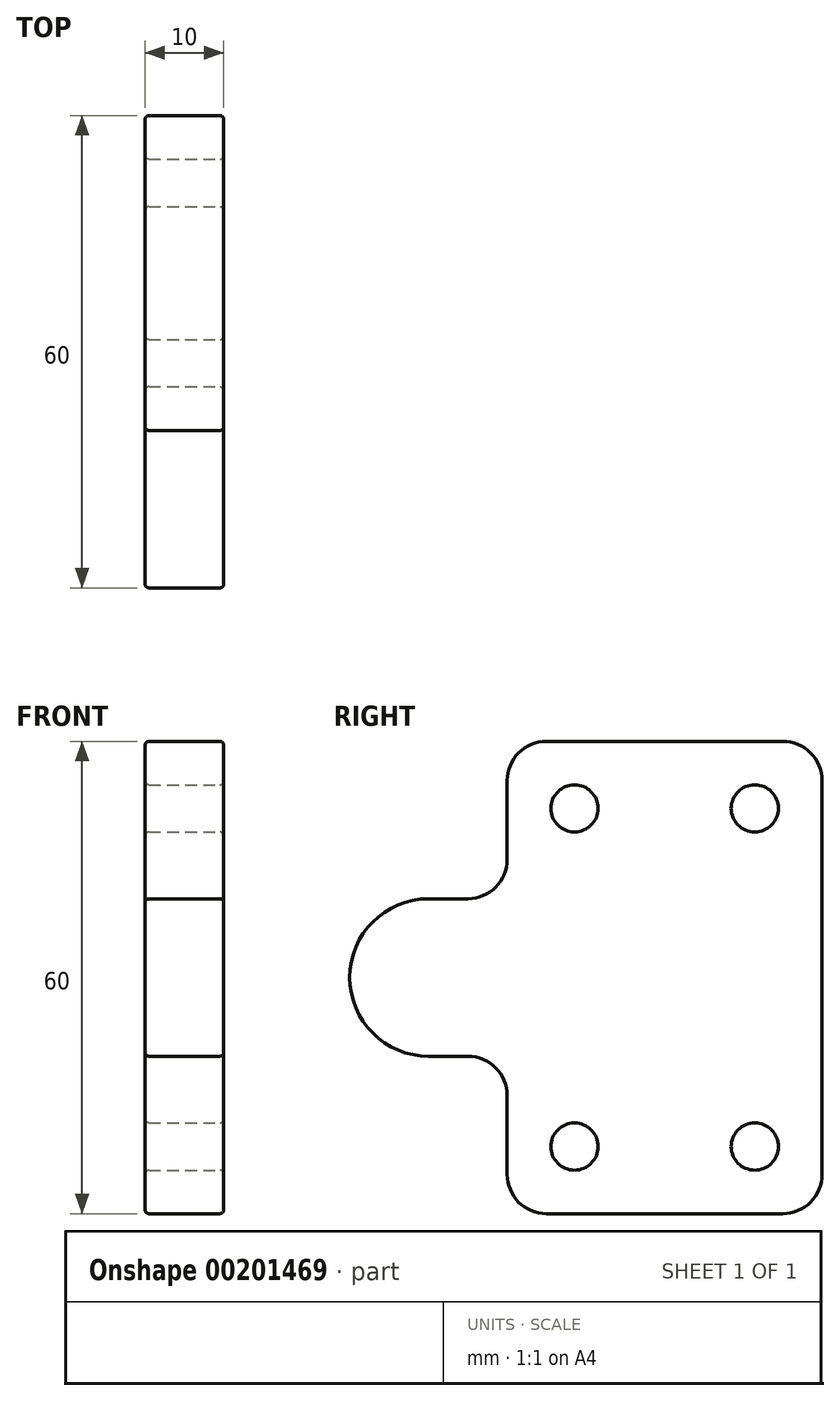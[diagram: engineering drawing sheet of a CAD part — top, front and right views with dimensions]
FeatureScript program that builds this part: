
annotation { "Feature Type Name" : "Feature", "Feature Type Description" : "" }
export const myFeature = defineFeature(function(context is Context, id is Id, definition is map)
    precondition{}
    {
        {
            var Q0;
            Q0=qCreatedBy(makeId("Right.planeOp"),FACE);
            var sketch = newSketch(context, id + "F0", { "sketchPlane" : qUnion([Q0])});
            skLineSegment(sketch, "E0.bottom", {"start": v(-20, -30) * mm, "end": v(20, -30) * mm});
            skLineSegment(sketch, "E0.top", {"start": v(-20, 30) * mm, "end": v(20, 30) * mm});
            skLineSegment(sketch, "E0.left", {"start": v(-20, -30) * mm, "end": v(-20, -15) * mm});
            skLineSegment(sketch, "E0.right", {"start": v(20, -30) * mm, "end": v(20, 30) * mm});
            skPoint(sketch, "E0.middle", {"position": v(0, 0) * mm});
            skArc(sketch, "E1", {"start": v(-30, 10) * mm, "mid": v(-40, 0) * mm, "end": v(-30, -10) * mm});
            skLineSegment(sketch, "E2", {"start": v(-30, 10) * mm, "end": v(-25, 10) * mm});
            skLineSegment(sketch, "E3", {"start": v(-30, -10) * mm, "end": v(-25, -10) * mm});
            skLineSegment(sketch, "E4.trimOffspring", {"start": v(-20, 15) * mm, "end": v(-20, 30) * mm});
            skPoint(sketch, "E5.visualSharp", {"position": v(-20, -10) * mm});
            skArc(sketch, "E5.filletArc", {"start": v(-20, -15) * mm, "mid": v(-21.46, -11.46) * mm, "end": v(-25, -10) * mm});
            skPoint(sketch, "E6.visualSharp", {"position": v(-20, 10) * mm});
            skArc(sketch, "E6.filletArc", {"start": v(-25, 10) * mm, "mid": v(-21.46, 11.46) * mm, "end": v(-20, 15) * mm});
            skSolve(sketch);
        }
        {
            var Q0;
            Q0=makeQuery(id+"F0.imprint","IMPRINT",FACE,{"disambiguationData":[TD([[makeQuery(id+"F0.imprint","IMPRINT",EDGE,{"derivedFrom":sQuery(id+"F0.wireOp",EDGE,"E0.bottom")}),1.0]])]});
            extrude(context, id + "F1", {"entities" : qUnion([Q0]), "depth" : 10 * mm});
        }
        {
            var Q0;
            Q0=makeQuery(id+"F1.opExtrude","SWEPT_EDGE",EDGE,{"disambiguationData":[OSD([sQuery(id+"F0.wireOp",EDGE,"E0.top"),sQuery(id+"F0.wireOp",EDGE,"E4.trimOffspring")])]});
            var Q1;
            Q1=makeQuery(id+"F1.opExtrude","SWEPT_EDGE",EDGE,{"disambiguationData":[OSD([sQuery(id+"F0.wireOp",EDGE,"E0.top"),sQuery(id+"F0.wireOp",EDGE,"E0.right")])]});
            var Q2;
            Q2=makeQuery(id+"F1.opExtrude","SWEPT_EDGE",EDGE,{"disambiguationData":[OSD([sQuery(id+"F0.wireOp",EDGE,"E0.bottom"),sQuery(id+"F0.wireOp",EDGE,"E0.right")])]});
            var Q3;
            Q3=makeQuery(id+"F1.opExtrude","SWEPT_EDGE",EDGE,{"disambiguationData":[OSD([sQuery(id+"F0.wireOp",EDGE,"E0.bottom"),sQuery(id+"F0.wireOp",EDGE,"E0.left")])]});
            fillet(context, id + "F2", {"entities" : qUnion([Q0, Q1, Q2, Q3]), "radius" : 5 * mm, "tangentPropagation" : true, "allowEdgeOverflow" : false});
        }
        {
            var Q0;
            Q0=makeQuery(id+"F1.opExtrude","CAP_FACE",FACE,{"disambiguationData":[OSD([sQuery(id+"F0.wireOp",EDGE,"E0.bottom"),sQuery(id+"F0.wireOp",EDGE,"E0.top"),sQuery(id+"F0.wireOp",EDGE,"E0.left"),sQuery(id+"F0.wireOp",EDGE,"E0.right"),sQuery(id+"F0.wireOp",EDGE,"E1"),sQuery(id+"F0.wireOp",EDGE,"E2"),sQuery(id+"F0.wireOp",EDGE,"E3"),sQuery(id+"F0.wireOp",EDGE,"E4.trimOffspring"),sQuery(id+"F0.wireOp",EDGE,"E5.filletArc"),sQuery(id+"F0.wireOp",EDGE,"E6.filletArc")])],"isStart":false});
            var sketch = newSketch(context, id + "F3", { "sketchPlane" : qUnion([Q0])});
            skPoint(sketch, "E7", {"position": v(7.84, 8.3) * mm});
            skSolve(sketch);
        }
        {
            var Q0;
            {var subQ6=sQuery(id+"F0.wireOp",EDGE,"E1");Q0=makeQuery(id+"F3.imprint","IMPRINT",FACE,{"disambiguationData":[TD([[makeQuery(id+"F3.imprint","IMPRINT",EDGE,{"derivedFrom":makeQuery(id+"F1.opExtrude","CAP_EDGE",EDGE,{"disambiguationData":[OSD([subQ6])],"isStart":false})}),1.0]])]});}
            var sketch = newSketch(context, id + "F4", { "sketchPlane" : qUnion([Q0])});
            skPoint(sketch, "E8", {"position": v(-11.45, 21.48) * mm});
            skLineSegment(sketch, "E9", {"start": v(-43.3, 0) * mm, "end": v(25.62, 0) * mm, "construction": true});
            skLineSegment(sketch, "E10", {"start": v(0, 34.37) * mm, "end": v(0, -34.73) * mm, "construction": true});
            skPoint(sketch, "E11.MirrorP", {"position": v(-11.45, -21.48) * mm});
            skPoint(sketch, "E12.MirrorP", {"position": v(11.45, -21.48) * mm});
            skPoint(sketch, "E13.MirrorP", {"position": v(11.45, 21.48) * mm});
            skSolve(sketch);
        }
        {
            var Q0;
            Q0=sQuery(id+"F4.wireOp",VERTEX,"E8");
            var Q1;
            Q1=sQuery(id+"F4.wireOp",VERTEX,"E13.MirrorP");
            var Q2;
            Q2=sQuery(id+"F4.wireOp",VERTEX,"E12.MirrorP");
            var Q3;
            Q3=sQuery(id+"F4.wireOp",VERTEX,"E11.MirrorP");
            var Q4;
            Q4=makeQuery(id+"F1.opExtrude","SWEPT_BODY",BODY,{"disambiguationData":[OSD([sQuery(id+"F0.wireOp",EDGE,"E0.bottom"),sQuery(id+"F0.wireOp",EDGE,"E0.top"),sQuery(id+"F0.wireOp",EDGE,"E0.left"),sQuery(id+"F0.wireOp",EDGE,"E0.right"),sQuery(id+"F0.wireOp",EDGE,"E1"),sQuery(id+"F0.wireOp",EDGE,"E2"),sQuery(id+"F0.wireOp",EDGE,"E3"),sQuery(id+"F0.wireOp",EDGE,"E4.trimOffspring"),sQuery(id+"F0.wireOp",EDGE,"E5.filletArc"),sQuery(id+"F0.wireOp",EDGE,"E6.filletArc")])]});
            hole(context, id + "F5", {"style" : HoleStyle.SIMPLE, "endStyle" : HoleEndStyle.THROUGH, "holeDiameter" : 6 * mm, "locations" : qUnion([Q0, Q1, Q2, Q3]), "scope" : qUnion([Q4]), "isTappedThrough" : true});
        }
        {
            var Q0;
            Q0=makeQuery(id+"F2.opFillet","BLEND_FACE",FACE,{"disambiguationData":[OSD([sQuery(id+"F0.wireOp",EDGE,"E0.bottom"),sQuery(id+"F0.wireOp",EDGE,"E0.left")])]});
            var Q1;
            {var subQ0=sQuery(id+"F0.wireOp",EDGE,"E0.left");var subQ1=sQuery(id+"F0.wireOp",EDGE,"E0.bottom");Q1=makeQuery(id+"F2.opFillet","BLEND_EDGE",EDGE,{"blendedFrom":[makeQuery(id+"F1.opExtrude","SWEPT_EDGE",EDGE,{"disambiguationData":[OSD([subQ1,subQ0])]}),makeQuery(id+"F1.opExtrude","CAP_FACE",FACE,{"disambiguationData":[OSD([subQ1,sQuery(id+"F0.wireOp",EDGE,"E0.top"),subQ0,sQuery(id+"F0.wireOp",EDGE,"E0.right"),sQuery(id+"F0.wireOp",EDGE,"E1"),sQuery(id+"F0.wireOp",EDGE,"E2"),sQuery(id+"F0.wireOp",EDGE,"E3"),sQuery(id+"F0.wireOp",EDGE,"E4.trimOffspring"),sQuery(id+"F0.wireOp",EDGE,"E5.filletArc"),sQuery(id+"F0.wireOp",EDGE,"E6.filletArc")])],"isStart":false})],"blendedInto":[makeQuery(id+"F1.opExtrude","CAP_FACE",FACE,{"disambiguationData":[OSD([subQ1,sQuery(id+"F0.wireOp",EDGE,"E0.top"),subQ0,sQuery(id+"F0.wireOp",EDGE,"E0.right"),sQuery(id+"F0.wireOp",EDGE,"E1"),sQuery(id+"F0.wireOp",EDGE,"E2"),sQuery(id+"F0.wireOp",EDGE,"E3"),sQuery(id+"F0.wireOp",EDGE,"E4.trimOffspring"),sQuery(id+"F0.wireOp",EDGE,"E5.filletArc"),sQuery(id+"F0.wireOp",EDGE,"E6.filletArc")])],"isStart":false})]});}
            var Q2;
            Q2=makeQuery(id+"F2.opFillet","BLEND_FACE",FACE,{"disambiguationData":[OSD([sQuery(id+"F0.wireOp",EDGE,"E0.top"),sQuery(id+"F0.wireOp",EDGE,"E4.trimOffspring")])]});
            var Q3;
            {var subQ0=sQuery(id+"F0.wireOp",EDGE,"E0.right");var subQ1=sQuery(id+"F0.wireOp",EDGE,"E0.bottom");Q3=makeQuery(id+"F2.opFillet","BLEND_EDGE",EDGE,{"blendedFrom":[makeQuery(id+"F1.opExtrude","SWEPT_EDGE",EDGE,{"disambiguationData":[OSD([subQ1,subQ0])]}),makeQuery(id+"F1.opExtrude","CAP_FACE",FACE,{"disambiguationData":[OSD([subQ1,sQuery(id+"F0.wireOp",EDGE,"E0.top"),sQuery(id+"F0.wireOp",EDGE,"E0.left"),subQ0,sQuery(id+"F0.wireOp",EDGE,"E1"),sQuery(id+"F0.wireOp",EDGE,"E2"),sQuery(id+"F0.wireOp",EDGE,"E3"),sQuery(id+"F0.wireOp",EDGE,"E4.trimOffspring"),sQuery(id+"F0.wireOp",EDGE,"E5.filletArc"),sQuery(id+"F0.wireOp",EDGE,"E6.filletArc")])],"isStart":false})],"blendedInto":[makeQuery(id+"F1.opExtrude","CAP_FACE",FACE,{"disambiguationData":[OSD([subQ1,sQuery(id+"F0.wireOp",EDGE,"E0.top"),sQuery(id+"F0.wireOp",EDGE,"E0.left"),subQ0,sQuery(id+"F0.wireOp",EDGE,"E1"),sQuery(id+"F0.wireOp",EDGE,"E2"),sQuery(id+"F0.wireOp",EDGE,"E3"),sQuery(id+"F0.wireOp",EDGE,"E4.trimOffspring"),sQuery(id+"F0.wireOp",EDGE,"E5.filletArc"),sQuery(id+"F0.wireOp",EDGE,"E6.filletArc")])],"isStart":false})]});}
            var Q4;
            Q4=makeQuery(id+"F2.opFillet","BLEND_FACE",FACE,{"disambiguationData":[OSD([sQuery(id+"F0.wireOp",EDGE,"E0.top"),sQuery(id+"F0.wireOp",EDGE,"E0.right")])]});
            var Q5;
            Q5=makeQuery(id+"F1.opExtrude","SWEPT_FACE",FACE,{"disambiguationData":[OSD([sQuery(id+"F0.wireOp",EDGE,"E1")])]});
            var Q6;
            Q6=makeQuery(id+"F1.opExtrude","SWEPT_FACE",FACE,{"disambiguationData":[OSD([sQuery(id+"F0.wireOp",EDGE,"E2")])]});
            var Q7;
            Q7=makeQuery(id+"F1.opExtrude","SWEPT_FACE",FACE,{"disambiguationData":[OSD([sQuery(id+"F0.wireOp",EDGE,"E0.bottom")])]});
            var Q8;
            Q8=makeQuery(id+"F1.opExtrude","SWEPT_FACE",FACE,{"disambiguationData":[OSD([sQuery(id+"F0.wireOp",EDGE,"E0.top")])]});
            var Q9;
            Q9=makeQuery(id+"F1.opExtrude","SWEPT_FACE",FACE,{"disambiguationData":[OSD([sQuery(id+"F0.wireOp",EDGE,"E3")])]});
            var Q10;
            Q10=makeQuery(id+"F1.opExtrude","SWEPT_FACE",FACE,{"disambiguationData":[OSD([sQuery(id+"F0.wireOp",EDGE,"E5.filletArc")])]});
            var Q11;
            {var subQ0=sQuery(id+"F0.wireOp",EDGE,"E0.right");var subQ1=sQuery(id+"F0.wireOp",EDGE,"E0.top");Q11=makeQuery(id+"F2.opFillet","BLEND_EDGE",EDGE,{"blendedFrom":[makeQuery(id+"F1.opExtrude","SWEPT_EDGE",EDGE,{"disambiguationData":[OSD([subQ1,subQ0])]}),makeQuery(id+"F1.opExtrude","CAP_FACE",FACE,{"disambiguationData":[OSD([sQuery(id+"F0.wireOp",EDGE,"E0.bottom"),subQ1,sQuery(id+"F0.wireOp",EDGE,"E0.left"),subQ0,sQuery(id+"F0.wireOp",EDGE,"E1"),sQuery(id+"F0.wireOp",EDGE,"E2"),sQuery(id+"F0.wireOp",EDGE,"E3"),sQuery(id+"F0.wireOp",EDGE,"E4.trimOffspring"),sQuery(id+"F0.wireOp",EDGE,"E5.filletArc"),sQuery(id+"F0.wireOp",EDGE,"E6.filletArc")])],"isStart":false})],"blendedInto":[makeQuery(id+"F1.opExtrude","CAP_FACE",FACE,{"disambiguationData":[OSD([sQuery(id+"F0.wireOp",EDGE,"E0.bottom"),subQ1,sQuery(id+"F0.wireOp",EDGE,"E0.left"),subQ0,sQuery(id+"F0.wireOp",EDGE,"E1"),sQuery(id+"F0.wireOp",EDGE,"E2"),sQuery(id+"F0.wireOp",EDGE,"E3"),sQuery(id+"F0.wireOp",EDGE,"E4.trimOffspring"),sQuery(id+"F0.wireOp",EDGE,"E5.filletArc"),sQuery(id+"F0.wireOp",EDGE,"E6.filletArc")])],"isStart":false})]});}
            var Q12;
            Q12=makeQuery(id+"F1.opExtrude","CAP_EDGE",EDGE,{"disambiguationData":[OSD([sQuery(id+"F0.wireOp",EDGE,"E1")])],"isStart":false});
            var Q13;
            Q13=makeQuery(id+"F2.opFillet","BLEND_FACE",FACE,{"disambiguationData":[OSD([sQuery(id+"F0.wireOp",EDGE,"E0.bottom"),sQuery(id+"F0.wireOp",EDGE,"E0.right")])]});
            var Q14;
            Q14=makeQuery(id+"F1.opExtrude","CAP_EDGE",EDGE,{"disambiguationData":[OSD([sQuery(id+"F0.wireOp",EDGE,"E5.filletArc")])],"isStart":false});
            var Q15;
            Q15=makeQuery(id+"F1.opExtrude","SWEPT_FACE",FACE,{"disambiguationData":[OSD([sQuery(id+"F0.wireOp",EDGE,"E0.left")])]});
            var Q16;
            {var subQ0=sQuery(id+"F0.wireOp",EDGE,"E4.trimOffspring");var subQ1=sQuery(id+"F0.wireOp",EDGE,"E0.top");Q16=makeQuery(id+"F2.opFillet","BLEND_EDGE",EDGE,{"blendedFrom":[makeQuery(id+"F1.opExtrude","SWEPT_EDGE",EDGE,{"disambiguationData":[OSD([subQ1,subQ0])]}),makeQuery(id+"F1.opExtrude","CAP_FACE",FACE,{"disambiguationData":[OSD([sQuery(id+"F0.wireOp",EDGE,"E0.bottom"),subQ1,sQuery(id+"F0.wireOp",EDGE,"E0.left"),sQuery(id+"F0.wireOp",EDGE,"E0.right"),sQuery(id+"F0.wireOp",EDGE,"E1"),sQuery(id+"F0.wireOp",EDGE,"E2"),sQuery(id+"F0.wireOp",EDGE,"E3"),subQ0,sQuery(id+"F0.wireOp",EDGE,"E5.filletArc"),sQuery(id+"F0.wireOp",EDGE,"E6.filletArc")])],"isStart":false})],"blendedInto":[makeQuery(id+"F1.opExtrude","CAP_FACE",FACE,{"disambiguationData":[OSD([sQuery(id+"F0.wireOp",EDGE,"E0.bottom"),subQ1,sQuery(id+"F0.wireOp",EDGE,"E0.left"),sQuery(id+"F0.wireOp",EDGE,"E0.right"),sQuery(id+"F0.wireOp",EDGE,"E1"),sQuery(id+"F0.wireOp",EDGE,"E2"),sQuery(id+"F0.wireOp",EDGE,"E3"),subQ0,sQuery(id+"F0.wireOp",EDGE,"E5.filletArc"),sQuery(id+"F0.wireOp",EDGE,"E6.filletArc")])],"isStart":false})]});}
            var Q17;
            Q17=makeQuery(id+"F1.opExtrude","SWEPT_FACE",FACE,{"disambiguationData":[OSD([sQuery(id+"F0.wireOp",EDGE,"E0.right")])]});
            var Q18;
            Q18=makeQuery(id+"F1.opExtrude","SWEPT_FACE",FACE,{"disambiguationData":[OSD([sQuery(id+"F0.wireOp",EDGE,"E4.trimOffspring")])]});
            var Q19;
            Q19=makeQuery(id+"F5.hole-0.boolean.opBoolean","COPY",FACE,{"derivedFrom":makeQuery(id+"F5.hole-0.opRevolve","SWEPT_FACE",FACE,{"disambiguationData":[OSD([sQuery(id+"F5.hole-0.sketch.wireOp",EDGE,"core_line_2")])]})});
            var Q20;
            Q20=makeQuery(id+"F5.hole-1.boolean.opBoolean","COPY",FACE,{"derivedFrom":makeQuery(id+"F5.hole-1.opRevolve","SWEPT_FACE",FACE,{"disambiguationData":[OSD([sQuery(id+"F5.hole-1.sketch.wireOp",EDGE,"core_line_2")])]})});
            var Q21;
            Q21=makeQuery(id+"F5.hole-1.boolean.opBoolean","COPY",EDGE,{"derivedFrom":makeQuery(id+"F5.hole-1.opRevolve","SWEPT_EDGE",EDGE,{"disambiguationData":[OSD([sQuery(id+"F5.hole-1.sketch.wireOp",EDGE,"core_line_2"),sQuery(id+"F5.hole-1.sketch.wireOp",EDGE,"core_line_3")])]})});
            var Q22;
            Q22=makeQuery(id+"F5.hole-0.boolean.opBoolean","COPY",EDGE,{"derivedFrom":makeQuery(id+"F5.hole-0.opRevolve","SWEPT_EDGE",EDGE,{"disambiguationData":[OSD([sQuery(id+"F5.hole-0.sketch.wireOp",EDGE,"core_line_2"),sQuery(id+"F5.hole-0.sketch.wireOp",EDGE,"core_line_3")])]})});
            var Q23;
            Q23=makeQuery(id+"F5.hole-3.boolean.opBoolean","COPY",FACE,{"derivedFrom":makeQuery(id+"F5.hole-3.opRevolve","SWEPT_FACE",FACE,{"disambiguationData":[OSD([sQuery(id+"F5.hole-3.sketch.wireOp",EDGE,"core_line_2")])]})});
            var Q24;
            Q24=makeQuery(id+"F5.hole-2.boolean.opBoolean","COPY",EDGE,{"derivedFrom":makeQuery(id+"F5.hole-2.opRevolve","SWEPT_EDGE",EDGE,{"disambiguationData":[OSD([sQuery(id+"F5.hole-2.sketch.wireOp",EDGE,"core_line_2"),sQuery(id+"F5.hole-2.sketch.wireOp",EDGE,"core_line_3")])]})});
            var Q25;
            Q25=makeQuery(id+"F5.hole-2.boolean.opBoolean","COPY",FACE,{"derivedFrom":makeQuery(id+"F5.hole-2.opRevolve","SWEPT_FACE",FACE,{"disambiguationData":[OSD([sQuery(id+"F5.hole-2.sketch.wireOp",EDGE,"core_line_2")])]})});
            var Q26;
            Q26=makeQuery(id+"F5.hole-3.boolean.opBoolean","COPY",EDGE,{"derivedFrom":makeQuery(id+"F5.hole-3.opRevolve","SWEPT_EDGE",EDGE,{"disambiguationData":[OSD([sQuery(id+"F5.hole-3.sketch.wireOp",EDGE,"core_line_2"),sQuery(id+"F5.hole-3.sketch.wireOp",EDGE,"core_line_3")])]})});
            var Q27;
            Q27=makeQuery(id+"F1.opExtrude","CAP_FACE",FACE,{"disambiguationData":[OSD([sQuery(id+"F0.wireOp",EDGE,"E0.bottom"),sQuery(id+"F0.wireOp",EDGE,"E0.top"),sQuery(id+"F0.wireOp",EDGE,"E0.left"),sQuery(id+"F0.wireOp",EDGE,"E0.right"),sQuery(id+"F0.wireOp",EDGE,"E1"),sQuery(id+"F0.wireOp",EDGE,"E2"),sQuery(id+"F0.wireOp",EDGE,"E3"),sQuery(id+"F0.wireOp",EDGE,"E4.trimOffspring"),sQuery(id+"F0.wireOp",EDGE,"E5.filletArc"),sQuery(id+"F0.wireOp",EDGE,"E6.filletArc")])],"isStart":false});
            var Q28;
            {var subQ0=sQuery(id+"F0.wireOp",EDGE,"E0.bottom");Q28=makeQuery(id+"F2.opFillet","BLEND_EDGE",EDGE,{"blendedFrom":[makeQuery(id+"F1.opExtrude","SWEPT_EDGE",EDGE,{"disambiguationData":[OSD([subQ0,sQuery(id+"F0.wireOp",EDGE,"E0.right")])]}),makeQuery(id+"F1.opExtrude","SWEPT_FACE",FACE,{"disambiguationData":[OSD([subQ0])]})],"blendedInto":[makeQuery(id+"F1.opExtrude","SWEPT_FACE",FACE,{"disambiguationData":[OSD([subQ0])]})]});}
            var Q29;
            {var subQ0=sQuery(id+"F0.wireOp",EDGE,"E0.bottom");Q29=makeQuery(id+"F2.opFillet","BLEND_EDGE",EDGE,{"blendedFrom":[makeQuery(id+"F1.opExtrude","SWEPT_EDGE",EDGE,{"disambiguationData":[OSD([subQ0,sQuery(id+"F0.wireOp",EDGE,"E0.left")])]}),makeQuery(id+"F1.opExtrude","SWEPT_FACE",FACE,{"disambiguationData":[OSD([subQ0])]})],"blendedInto":[makeQuery(id+"F1.opExtrude","SWEPT_FACE",FACE,{"disambiguationData":[OSD([subQ0])]})]});}
            var Q30;
            Q30=makeQuery(id+"F1.opExtrude","SWEPT_EDGE",EDGE,{"disambiguationData":[OSD([sQuery(id+"F0.wireOp",EDGE,"E1"),sQuery(id+"F0.wireOp",EDGE,"E3")])]});
            var Q31;
            {var subQ0=sQuery(id+"F0.wireOp",EDGE,"E0.left");Q31=makeQuery(id+"F2.opFillet","BLEND_EDGE",EDGE,{"blendedFrom":[makeQuery(id+"F1.opExtrude","SWEPT_EDGE",EDGE,{"disambiguationData":[OSD([sQuery(id+"F0.wireOp",EDGE,"E0.bottom"),subQ0])]}),makeQuery(id+"F1.opExtrude","SWEPT_FACE",FACE,{"disambiguationData":[OSD([subQ0])]})],"blendedInto":[makeQuery(id+"F1.opExtrude","SWEPT_FACE",FACE,{"disambiguationData":[OSD([subQ0])]})]});}
            var Q32;
            {var subQ0=sQuery(id+"F0.wireOp",EDGE,"E0.right");Q32=makeQuery(id+"F2.opFillet","BLEND_EDGE",EDGE,{"blendedFrom":[makeQuery(id+"F1.opExtrude","SWEPT_EDGE",EDGE,{"disambiguationData":[OSD([sQuery(id+"F0.wireOp",EDGE,"E0.top"),subQ0])]}),makeQuery(id+"F1.opExtrude","SWEPT_FACE",FACE,{"disambiguationData":[OSD([subQ0])]})],"blendedInto":[makeQuery(id+"F1.opExtrude","SWEPT_FACE",FACE,{"disambiguationData":[OSD([subQ0])]})]});}
            var Q33;
            {var subQ0=sQuery(id+"F0.wireOp",EDGE,"E0.left");var subQ1=sQuery(id+"F0.wireOp",EDGE,"E0.bottom");Q33=makeQuery(id+"F2.opFillet","BLEND_EDGE",EDGE,{"blendedFrom":[makeQuery(id+"F1.opExtrude","SWEPT_EDGE",EDGE,{"disambiguationData":[OSD([subQ1,subQ0])]}),makeQuery(id+"F1.opExtrude","CAP_FACE",FACE,{"disambiguationData":[OSD([subQ1,sQuery(id+"F0.wireOp",EDGE,"E0.top"),subQ0,sQuery(id+"F0.wireOp",EDGE,"E0.right"),sQuery(id+"F0.wireOp",EDGE,"E1"),sQuery(id+"F0.wireOp",EDGE,"E2"),sQuery(id+"F0.wireOp",EDGE,"E3"),sQuery(id+"F0.wireOp",EDGE,"E4.trimOffspring"),sQuery(id+"F0.wireOp",EDGE,"E5.filletArc"),sQuery(id+"F0.wireOp",EDGE,"E6.filletArc")])],"isStart":true})],"blendedInto":[makeQuery(id+"F1.opExtrude","CAP_FACE",FACE,{"disambiguationData":[OSD([subQ1,sQuery(id+"F0.wireOp",EDGE,"E0.top"),subQ0,sQuery(id+"F0.wireOp",EDGE,"E0.right"),sQuery(id+"F0.wireOp",EDGE,"E1"),sQuery(id+"F0.wireOp",EDGE,"E2"),sQuery(id+"F0.wireOp",EDGE,"E3"),sQuery(id+"F0.wireOp",EDGE,"E4.trimOffspring"),sQuery(id+"F0.wireOp",EDGE,"E5.filletArc"),sQuery(id+"F0.wireOp",EDGE,"E6.filletArc")])],"isStart":true})]});}
            var Q34;
            Q34=makeQuery(id+"F1.opExtrude","SWEPT_EDGE",EDGE,{"disambiguationData":[OSD([sQuery(id+"F0.wireOp",EDGE,"E1"),sQuery(id+"F0.wireOp",EDGE,"E2")])]});
            var Q35;
            {var subQ0=sQuery(id+"F0.wireOp",EDGE,"E0.right");var subQ1=sQuery(id+"F0.wireOp",EDGE,"E0.bottom");Q35=makeQuery(id+"F2.opFillet","BLEND_EDGE",EDGE,{"blendedFrom":[makeQuery(id+"F1.opExtrude","SWEPT_EDGE",EDGE,{"disambiguationData":[OSD([subQ1,subQ0])]}),makeQuery(id+"F1.opExtrude","CAP_FACE",FACE,{"disambiguationData":[OSD([subQ1,sQuery(id+"F0.wireOp",EDGE,"E0.top"),sQuery(id+"F0.wireOp",EDGE,"E0.left"),subQ0,sQuery(id+"F0.wireOp",EDGE,"E1"),sQuery(id+"F0.wireOp",EDGE,"E2"),sQuery(id+"F0.wireOp",EDGE,"E3"),sQuery(id+"F0.wireOp",EDGE,"E4.trimOffspring"),sQuery(id+"F0.wireOp",EDGE,"E5.filletArc"),sQuery(id+"F0.wireOp",EDGE,"E6.filletArc")])],"isStart":true})],"blendedInto":[makeQuery(id+"F1.opExtrude","CAP_FACE",FACE,{"disambiguationData":[OSD([subQ1,sQuery(id+"F0.wireOp",EDGE,"E0.top"),sQuery(id+"F0.wireOp",EDGE,"E0.left"),subQ0,sQuery(id+"F0.wireOp",EDGE,"E1"),sQuery(id+"F0.wireOp",EDGE,"E2"),sQuery(id+"F0.wireOp",EDGE,"E3"),sQuery(id+"F0.wireOp",EDGE,"E4.trimOffspring"),sQuery(id+"F0.wireOp",EDGE,"E5.filletArc"),sQuery(id+"F0.wireOp",EDGE,"E6.filletArc")])],"isStart":true})]});}
            var Q36;
            {var subQ0=sQuery(id+"F0.wireOp",EDGE,"E0.top");Q36=makeQuery(id+"F2.opFillet","BLEND_EDGE",EDGE,{"blendedFrom":[makeQuery(id+"F1.opExtrude","SWEPT_EDGE",EDGE,{"disambiguationData":[OSD([subQ0,sQuery(id+"F0.wireOp",EDGE,"E0.right")])]}),makeQuery(id+"F1.opExtrude","SWEPT_FACE",FACE,{"disambiguationData":[OSD([subQ0])]})],"blendedInto":[makeQuery(id+"F1.opExtrude","SWEPT_FACE",FACE,{"disambiguationData":[OSD([subQ0])]})]});}
            var Q37;
            Q37=makeQuery(id+"F1.opExtrude","CAP_EDGE",EDGE,{"disambiguationData":[OSD([sQuery(id+"F0.wireOp",EDGE,"E6.filletArc")])],"isStart":false});
            var Q38;
            Q38=makeQuery(id+"F1.opExtrude","CAP_EDGE",EDGE,{"disambiguationData":[OSD([sQuery(id+"F0.wireOp",EDGE,"E1")])],"isStart":true});
            var Q39;
            Q39=makeQuery(id+"F1.opExtrude","CAP_EDGE",EDGE,{"disambiguationData":[OSD([sQuery(id+"F0.wireOp",EDGE,"E2")])],"isStart":false});
            var Q40;
            Q40=makeQuery(id+"F1.opExtrude","CAP_EDGE",EDGE,{"disambiguationData":[OSD([sQuery(id+"F0.wireOp",EDGE,"E3")])],"isStart":false});
            var Q41;
            Q41=makeQuery(id+"F1.opExtrude","CAP_EDGE",EDGE,{"disambiguationData":[OSD([sQuery(id+"F0.wireOp",EDGE,"E5.filletArc")])],"isStart":true});
            var Q42;
            {var subQ0=sQuery(id+"F0.wireOp",EDGE,"E4.trimOffspring");var subQ1=sQuery(id+"F0.wireOp",EDGE,"E0.top");Q42=makeQuery(id+"F2.opFillet","BLEND_EDGE",EDGE,{"blendedFrom":[makeQuery(id+"F1.opExtrude","SWEPT_EDGE",EDGE,{"disambiguationData":[OSD([subQ1,subQ0])]}),makeQuery(id+"F1.opExtrude","CAP_FACE",FACE,{"disambiguationData":[OSD([sQuery(id+"F0.wireOp",EDGE,"E0.bottom"),subQ1,sQuery(id+"F0.wireOp",EDGE,"E0.left"),sQuery(id+"F0.wireOp",EDGE,"E0.right"),sQuery(id+"F0.wireOp",EDGE,"E1"),sQuery(id+"F0.wireOp",EDGE,"E2"),sQuery(id+"F0.wireOp",EDGE,"E3"),subQ0,sQuery(id+"F0.wireOp",EDGE,"E5.filletArc"),sQuery(id+"F0.wireOp",EDGE,"E6.filletArc")])],"isStart":true})],"blendedInto":[makeQuery(id+"F1.opExtrude","CAP_FACE",FACE,{"disambiguationData":[OSD([sQuery(id+"F0.wireOp",EDGE,"E0.bottom"),subQ1,sQuery(id+"F0.wireOp",EDGE,"E0.left"),sQuery(id+"F0.wireOp",EDGE,"E0.right"),sQuery(id+"F0.wireOp",EDGE,"E1"),sQuery(id+"F0.wireOp",EDGE,"E2"),sQuery(id+"F0.wireOp",EDGE,"E3"),subQ0,sQuery(id+"F0.wireOp",EDGE,"E5.filletArc"),sQuery(id+"F0.wireOp",EDGE,"E6.filletArc")])],"isStart":true})]});}
            var Q43;
            {var subQ0=sQuery(id+"F0.wireOp",EDGE,"E0.top");Q43=makeQuery(id+"F2.opFillet","BLEND_EDGE",EDGE,{"blendedFrom":[makeQuery(id+"F1.opExtrude","SWEPT_EDGE",EDGE,{"disambiguationData":[OSD([subQ0,sQuery(id+"F0.wireOp",EDGE,"E4.trimOffspring")])]}),makeQuery(id+"F1.opExtrude","SWEPT_FACE",FACE,{"disambiguationData":[OSD([subQ0])]})],"blendedInto":[makeQuery(id+"F1.opExtrude","SWEPT_FACE",FACE,{"disambiguationData":[OSD([subQ0])]})]});}
            var Q44;
            {var subQ0=sQuery(id+"F0.wireOp",EDGE,"E4.trimOffspring");Q44=makeQuery(id+"F2.opFillet","BLEND_EDGE",EDGE,{"blendedFrom":[makeQuery(id+"F1.opExtrude","SWEPT_EDGE",EDGE,{"disambiguationData":[OSD([sQuery(id+"F0.wireOp",EDGE,"E0.top"),subQ0])]}),makeQuery(id+"F1.opExtrude","SWEPT_FACE",FACE,{"disambiguationData":[OSD([subQ0])]})],"blendedInto":[makeQuery(id+"F1.opExtrude","SWEPT_FACE",FACE,{"disambiguationData":[OSD([subQ0])]})]});}
            var Q45;
            {var subQ0=sQuery(id+"F0.wireOp",EDGE,"E0.right");var subQ1=sQuery(id+"F0.wireOp",EDGE,"E0.top");Q45=makeQuery(id+"F2.opFillet","BLEND_EDGE",EDGE,{"blendedFrom":[makeQuery(id+"F1.opExtrude","SWEPT_EDGE",EDGE,{"disambiguationData":[OSD([subQ1,subQ0])]}),makeQuery(id+"F1.opExtrude","CAP_FACE",FACE,{"disambiguationData":[OSD([sQuery(id+"F0.wireOp",EDGE,"E0.bottom"),subQ1,sQuery(id+"F0.wireOp",EDGE,"E0.left"),subQ0,sQuery(id+"F0.wireOp",EDGE,"E1"),sQuery(id+"F0.wireOp",EDGE,"E2"),sQuery(id+"F0.wireOp",EDGE,"E3"),sQuery(id+"F0.wireOp",EDGE,"E4.trimOffspring"),sQuery(id+"F0.wireOp",EDGE,"E5.filletArc"),sQuery(id+"F0.wireOp",EDGE,"E6.filletArc")])],"isStart":true})],"blendedInto":[makeQuery(id+"F1.opExtrude","CAP_FACE",FACE,{"disambiguationData":[OSD([sQuery(id+"F0.wireOp",EDGE,"E0.bottom"),subQ1,sQuery(id+"F0.wireOp",EDGE,"E0.left"),subQ0,sQuery(id+"F0.wireOp",EDGE,"E1"),sQuery(id+"F0.wireOp",EDGE,"E2"),sQuery(id+"F0.wireOp",EDGE,"E3"),sQuery(id+"F0.wireOp",EDGE,"E4.trimOffspring"),sQuery(id+"F0.wireOp",EDGE,"E5.filletArc"),sQuery(id+"F0.wireOp",EDGE,"E6.filletArc")])],"isStart":true})]});}
            var Q46;
            Q46=makeQuery(id+"F1.opExtrude","CAP_EDGE",EDGE,{"disambiguationData":[OSD([sQuery(id+"F0.wireOp",EDGE,"E0.bottom")])],"isStart":false});
            var Q47;
            Q47=makeQuery(id+"F1.opExtrude","CAP_EDGE",EDGE,{"disambiguationData":[OSD([sQuery(id+"F0.wireOp",EDGE,"E0.top")])],"isStart":false});
            var Q48;
            Q48=makeQuery(id+"F1.opExtrude","CAP_EDGE",EDGE,{"disambiguationData":[OSD([sQuery(id+"F0.wireOp",EDGE,"E0.left")])],"isStart":false});
            var Q49;
            Q49=makeQuery(id+"F1.opExtrude","CAP_EDGE",EDGE,{"disambiguationData":[OSD([sQuery(id+"F0.wireOp",EDGE,"E4.trimOffspring")])],"isStart":false});
            var Q50;
            Q50=makeQuery(id+"F5.hole-1.boolean.opBoolean","INTERSECT",EDGE,{"derivedFrom":[makeQuery(id+"F1.opExtrude","CAP_FACE",FACE,{"disambiguationData":[OSD([sQuery(id+"F0.wireOp",EDGE,"E0.bottom"),sQuery(id+"F0.wireOp",EDGE,"E0.top"),sQuery(id+"F0.wireOp",EDGE,"E0.left"),sQuery(id+"F0.wireOp",EDGE,"E0.right"),sQuery(id+"F0.wireOp",EDGE,"E1"),sQuery(id+"F0.wireOp",EDGE,"E2"),sQuery(id+"F0.wireOp",EDGE,"E3"),sQuery(id+"F0.wireOp",EDGE,"E4.trimOffspring"),sQuery(id+"F0.wireOp",EDGE,"E5.filletArc"),sQuery(id+"F0.wireOp",EDGE,"E6.filletArc")])],"isStart":true}),makeQuery(id+"F5.hole-1.opRevolve","SWEPT_FACE",FACE,{"disambiguationData":[OSD([sQuery(id+"F5.hole-1.sketch.wireOp",EDGE,"core_line_2")])]})]});
            var Q51;
            Q51=makeQuery(id+"F5.hole-0.boolean.opBoolean","INTERSECT",EDGE,{"derivedFrom":[makeQuery(id+"F1.opExtrude","CAP_FACE",FACE,{"disambiguationData":[OSD([sQuery(id+"F0.wireOp",EDGE,"E0.bottom"),sQuery(id+"F0.wireOp",EDGE,"E0.top"),sQuery(id+"F0.wireOp",EDGE,"E0.left"),sQuery(id+"F0.wireOp",EDGE,"E0.right"),sQuery(id+"F0.wireOp",EDGE,"E1"),sQuery(id+"F0.wireOp",EDGE,"E2"),sQuery(id+"F0.wireOp",EDGE,"E3"),sQuery(id+"F0.wireOp",EDGE,"E4.trimOffspring"),sQuery(id+"F0.wireOp",EDGE,"E5.filletArc"),sQuery(id+"F0.wireOp",EDGE,"E6.filletArc")])],"isStart":true}),makeQuery(id+"F5.hole-0.opRevolve","SWEPT_FACE",FACE,{"disambiguationData":[OSD([sQuery(id+"F5.hole-0.sketch.wireOp",EDGE,"core_line_2")])]})]});
            var Q52;
            Q52=makeQuery(id+"F5.hole-3.boolean.opBoolean","INTERSECT",EDGE,{"derivedFrom":[makeQuery(id+"F1.opExtrude","CAP_FACE",FACE,{"disambiguationData":[OSD([sQuery(id+"F0.wireOp",EDGE,"E0.bottom"),sQuery(id+"F0.wireOp",EDGE,"E0.top"),sQuery(id+"F0.wireOp",EDGE,"E0.left"),sQuery(id+"F0.wireOp",EDGE,"E0.right"),sQuery(id+"F0.wireOp",EDGE,"E1"),sQuery(id+"F0.wireOp",EDGE,"E2"),sQuery(id+"F0.wireOp",EDGE,"E3"),sQuery(id+"F0.wireOp",EDGE,"E4.trimOffspring"),sQuery(id+"F0.wireOp",EDGE,"E5.filletArc"),sQuery(id+"F0.wireOp",EDGE,"E6.filletArc")])],"isStart":true}),makeQuery(id+"F5.hole-3.opRevolve","SWEPT_FACE",FACE,{"disambiguationData":[OSD([sQuery(id+"F5.hole-3.sketch.wireOp",EDGE,"core_line_2")])]})]});
            var Q53;
            Q53=makeQuery(id+"F5.hole-2.boolean.opBoolean","INTERSECT",EDGE,{"derivedFrom":[makeQuery(id+"F1.opExtrude","CAP_FACE",FACE,{"disambiguationData":[OSD([sQuery(id+"F0.wireOp",EDGE,"E0.bottom"),sQuery(id+"F0.wireOp",EDGE,"E0.top"),sQuery(id+"F0.wireOp",EDGE,"E0.left"),sQuery(id+"F0.wireOp",EDGE,"E0.right"),sQuery(id+"F0.wireOp",EDGE,"E1"),sQuery(id+"F0.wireOp",EDGE,"E2"),sQuery(id+"F0.wireOp",EDGE,"E3"),sQuery(id+"F0.wireOp",EDGE,"E4.trimOffspring"),sQuery(id+"F0.wireOp",EDGE,"E5.filletArc"),sQuery(id+"F0.wireOp",EDGE,"E6.filletArc")])],"isStart":true}),makeQuery(id+"F5.hole-2.opRevolve","SWEPT_FACE",FACE,{"disambiguationData":[OSD([sQuery(id+"F5.hole-2.sketch.wireOp",EDGE,"core_line_2")])]})]});
            var Q54;
            Q54=makeQuery(id+"F1.opExtrude","CAP_FACE",FACE,{"disambiguationData":[OSD([sQuery(id+"F0.wireOp",EDGE,"E0.bottom"),sQuery(id+"F0.wireOp",EDGE,"E0.top"),sQuery(id+"F0.wireOp",EDGE,"E0.left"),sQuery(id+"F0.wireOp",EDGE,"E0.right"),sQuery(id+"F0.wireOp",EDGE,"E1"),sQuery(id+"F0.wireOp",EDGE,"E2"),sQuery(id+"F0.wireOp",EDGE,"E3"),sQuery(id+"F0.wireOp",EDGE,"E4.trimOffspring"),sQuery(id+"F0.wireOp",EDGE,"E5.filletArc"),sQuery(id+"F0.wireOp",EDGE,"E6.filletArc")])],"isStart":true});
            var Q55;
            Q55=makeQuery(id+"F1.opExtrude","SWEPT_EDGE",EDGE,{"disambiguationData":[OSD([sQuery(id+"F0.wireOp",EDGE,"E0.left"),sQuery(id+"F0.wireOp",EDGE,"E5.filletArc")])]});
            var Q56;
            Q56=makeQuery(id+"F1.opExtrude","SWEPT_EDGE",EDGE,{"disambiguationData":[OSD([sQuery(id+"F0.wireOp",EDGE,"E2"),sQuery(id+"F0.wireOp",EDGE,"E6.filletArc")])]});
            var Q57;
            {var subQ0=sQuery(id+"F0.wireOp",EDGE,"E0.right");Q57=makeQuery(id+"F2.opFillet","BLEND_EDGE",EDGE,{"blendedFrom":[makeQuery(id+"F1.opExtrude","SWEPT_EDGE",EDGE,{"disambiguationData":[OSD([sQuery(id+"F0.wireOp",EDGE,"E0.bottom"),subQ0])]}),makeQuery(id+"F1.opExtrude","SWEPT_FACE",FACE,{"disambiguationData":[OSD([subQ0])]})],"blendedInto":[makeQuery(id+"F1.opExtrude","SWEPT_FACE",FACE,{"disambiguationData":[OSD([subQ0])]})]});}
            var Q58;
            Q58=makeQuery(id+"F1.opExtrude","SWEPT_EDGE",EDGE,{"disambiguationData":[OSD([sQuery(id+"F0.wireOp",EDGE,"E3"),sQuery(id+"F0.wireOp",EDGE,"E5.filletArc")])]});
            var Q59;
            Q59=makeQuery(id+"F1.opExtrude","SWEPT_EDGE",EDGE,{"disambiguationData":[OSD([sQuery(id+"F0.wireOp",EDGE,"E4.trimOffspring"),sQuery(id+"F0.wireOp",EDGE,"E6.filletArc")])]});
            var Q60;
            Q60=makeQuery(id+"F1.opExtrude","SWEPT_FACE",FACE,{"disambiguationData":[OSD([sQuery(id+"F0.wireOp",EDGE,"E6.filletArc")])]});
            var Q61;
            Q61=makeQuery(id+"F1.opExtrude","CAP_EDGE",EDGE,{"disambiguationData":[OSD([sQuery(id+"F0.wireOp",EDGE,"E2")])],"isStart":true});
            var Q62;
            Q62=makeQuery(id+"F1.opExtrude","CAP_EDGE",EDGE,{"disambiguationData":[OSD([sQuery(id+"F0.wireOp",EDGE,"E3")])],"isStart":true});
            var Q63;
            Q63=makeQuery(id+"F1.opExtrude","CAP_EDGE",EDGE,{"disambiguationData":[OSD([sQuery(id+"F0.wireOp",EDGE,"E0.bottom")])],"isStart":true});
            var Q64;
            Q64=makeQuery(id+"F1.opExtrude","CAP_EDGE",EDGE,{"disambiguationData":[OSD([sQuery(id+"F0.wireOp",EDGE,"E0.top")])],"isStart":true});
            var Q65;
            Q65=makeQuery(id+"F1.opExtrude","CAP_EDGE",EDGE,{"disambiguationData":[OSD([sQuery(id+"F0.wireOp",EDGE,"E0.left")])],"isStart":true});
            var Q66;
            Q66=makeQuery(id+"F1.opExtrude","CAP_EDGE",EDGE,{"disambiguationData":[OSD([sQuery(id+"F0.wireOp",EDGE,"E0.right")])],"isStart":false});
            var Q67;
            Q67=makeQuery(id+"F1.opExtrude","CAP_EDGE",EDGE,{"disambiguationData":[OSD([sQuery(id+"F0.wireOp",EDGE,"E4.trimOffspring")])],"isStart":true});
            var Q68;
            Q68=makeQuery(id+"F1.opExtrude","CAP_EDGE",EDGE,{"disambiguationData":[OSD([sQuery(id+"F0.wireOp",EDGE,"E6.filletArc")])],"isStart":true});
            var Q69;
            Q69=makeQuery(id+"F1.opExtrude","CAP_EDGE",EDGE,{"disambiguationData":[OSD([sQuery(id+"F0.wireOp",EDGE,"E0.right")])],"isStart":true});
            fillet(context, id + "F6", {"entities" : qUnion([Q0, Q1, Q2, Q3, Q4, Q5, Q6, Q7, Q8, Q9, Q10, Q11, Q12, Q13, Q14, Q15, Q16, Q17, Q18, Q19, Q20, Q21, Q22, Q23, Q24, Q25, Q26, Q27, Q28, Q29, Q30, Q31, Q32, Q33, Q34, Q35, Q36, Q37, Q38, Q39, Q40, Q41, Q42, Q43, Q44, Q45, Q46, Q47, Q48, Q49, Q50, Q51, Q52, Q53, Q54, Q55, Q56, Q57, Q58, Q59, Q60, Q61, Q62, Q63, Q64, Q65, Q66, Q67, Q68, Q69]), "radius" : 0.5 * mm, "tangentPropagation" : true, "allowEdgeOverflow" : false});
        }
    });
